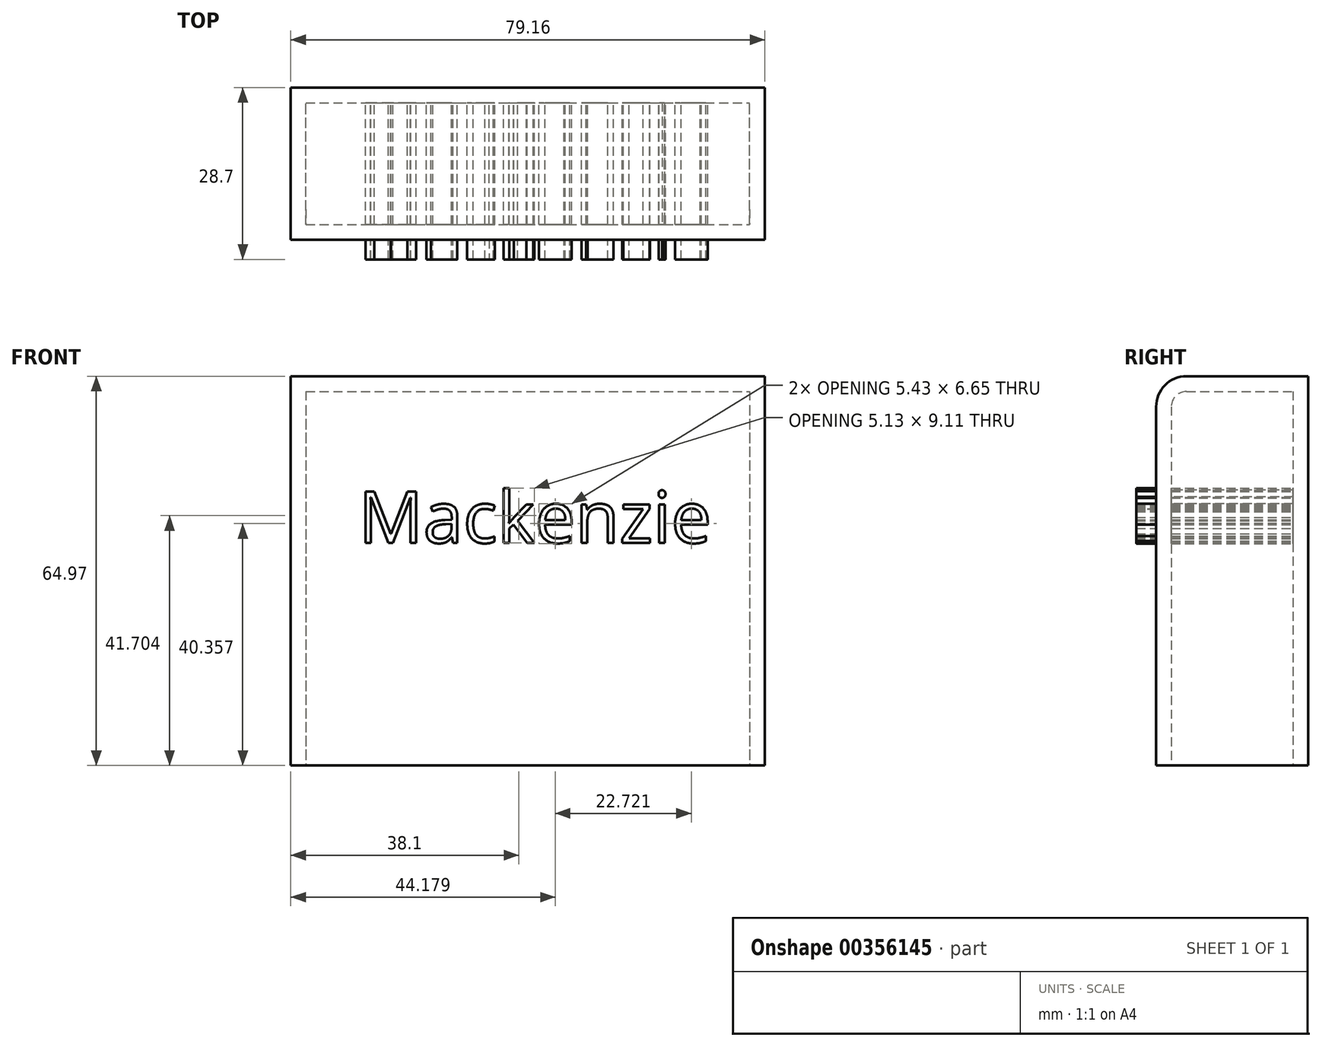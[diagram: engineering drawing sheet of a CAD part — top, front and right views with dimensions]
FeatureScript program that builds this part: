
annotation { "Feature Type Name" : "Feature", "Feature Type Description" : "" }
export const myFeature = defineFeature(function(context is Context, id is Id, definition is map)
    precondition{}
    {
        {
            var Q0;
            Q0=qCreatedBy(makeId("Front.planeOp"),FACE);
            var sketch = newSketch(context, id + "F0", { "sketchPlane" : qUnion([Q0])});
            skLineSegment(sketch, "E0.bottom", {"start": v(-40.29, 27.52) * mm, "end": v(38.87, 27.52) * mm});
            skLineSegment(sketch, "E0.top", {"start": v(-40.29, -37.45) * mm, "end": v(38.87, -37.45) * mm});
            skLineSegment(sketch, "E0.left", {"start": v(-40.29, 27.52) * mm, "end": v(-40.29, -37.45) * mm});
            skLineSegment(sketch, "E0.right", {"start": v(38.87, 27.52) * mm, "end": v(38.87, -37.45) * mm});
            skSolve(sketch);
        }
        {
            var Q0;
            Q0=makeQuery(id+"F0.imprint","IMPRINT",FACE,{"disambiguationData":[TD([[makeQuery(id+"F0.imprint","IMPRINT",EDGE,{"derivedFrom":sQuery(id+"F0.wireOp",EDGE,"E0.bottom")}),-1.0]])]});
            extrude(context, id + "F1", {"entities" : qUnion([Q0]), "depth" : 25.4 * mm});
        }
        {
            var Q0;
            Q0=makeQuery(id+"F1.opExtrude","CAP_EDGE",EDGE,{"disambiguationData":[OSD([sQuery(id+"F0.wireOp",EDGE,"E0.bottom")])],"isStart":false});
            fillet(context, id + "F2", {"entities" : qUnion([Q0]), "radius" : 5.08 * mm, "tangentPropagation" : true, "allowEdgeOverflow" : false});
        }
        {
            var Q0;
            Q0=makeQuery(id+"F1.opExtrude","SWEPT_FACE",FACE,{"disambiguationData":[OSD([sQuery(id+"F0.wireOp",EDGE,"E0.top")])]});
            shell(context, id + "F3", {"entities" : qUnion([Q0]), "thickness" : 2.54 * mm});
        }
        {
            var Q0;
            Q0=qCreatedBy(makeId("Front.planeOp"),FACE);
            var sketch = newSketch(context, id + "F4", { "sketchPlane" : qUnion([Q0])});
            skText(sketch, "E1", { "text": "Mackenzie", "fontName": "OpenSans-Regular.ttf"});
            const initialGuessF4  = {"E1": [-0.02898, -0.0003, 1, 0, 0.00863]};
            skSetInitialGuess(sketch, initialGuessF4);
            skSolve(sketch);
        }
        {
            var Q0;
            Q0 = qSketchRegion(id + "F4", true);
            extrude(context, id + "F5", {"entities" : qUnion([Q0]), "operationType" : NewBodyOperationType.ADD, "depth" : 28.7 * mm});
        }
    });
